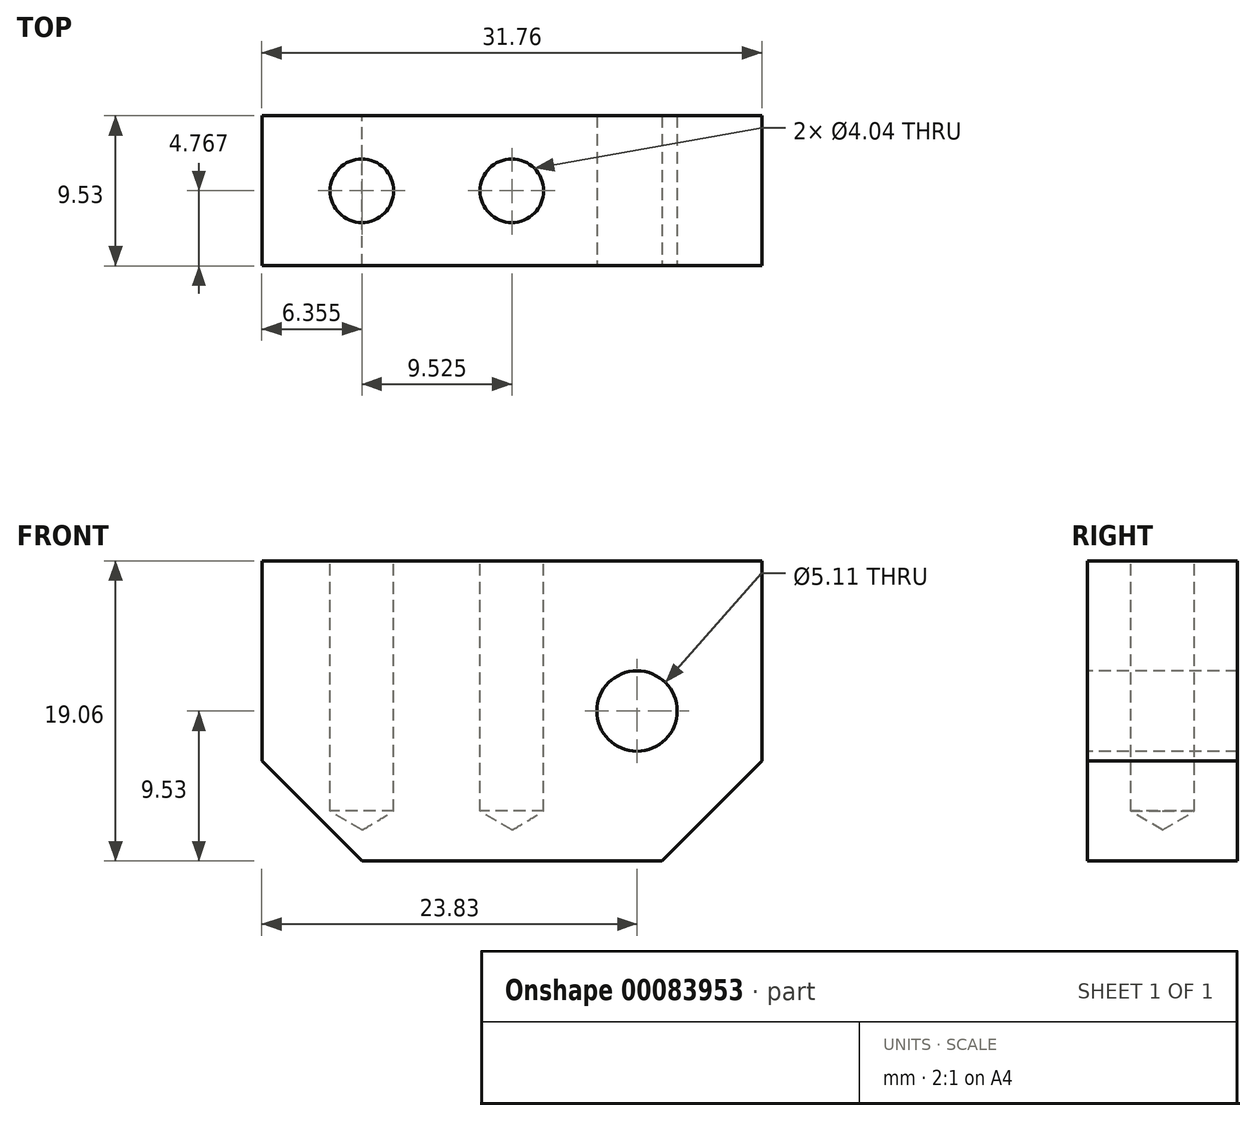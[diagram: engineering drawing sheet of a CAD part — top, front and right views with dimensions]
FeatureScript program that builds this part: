
annotation { "Feature Type Name" : "Feature", "Feature Type Description" : "" }
export const myFeature = defineFeature(function(context is Context, id is Id, definition is map)
    precondition{}
    {
        {
            var Q0;
            Q0=qCreatedBy(makeId("Front.planeOp"),FACE);
            var sketch = newSketch(context, id + "F0", { "sketchPlane" : qUnion([Q0])});
            skLineSegment(sketch, "E0.bottom", {"start": v(15.88, -9.52) * mm, "end": v(-15.88, -9.53) * mm});
            skLineSegment(sketch, "E0.top", {"start": v(15.88, 9.53) * mm, "end": v(-15.88, 9.52) * mm});
            skLineSegment(sketch, "E0.left", {"start": v(15.88, -9.52) * mm, "end": v(15.88, 9.53) * mm});
            skLineSegment(sketch, "E0.right", {"start": v(-15.88, -9.53) * mm, "end": v(-15.88, 9.52) * mm});
            skPoint(sketch, "E0.middle", {"position": v(0, 0) * mm});
            skSolve(sketch);
        }
        {
            var Q0;
            Q0=makeQuery(id+"F0.imprint","IMPRINT",FACE,{"disambiguationData":[TD([[makeQuery(id+"F0.imprint","IMPRINT",EDGE,{"derivedFrom":sQuery(id+"F0.wireOp",EDGE,"E0.bottom")}),-1.0]])]});
            extrude(context, id + "F1", {"entities" : qUnion([Q0]), "depth" : 9.52 * mm});
        }
        {
            var Q0;
            Q0=makeQuery(id+"F1.opExtrude","CAP_FACE",FACE,{"disambiguationData":[OSD([sQuery(id+"F0.wireOp",EDGE,"E0.bottom"),sQuery(id+"F0.wireOp",EDGE,"E0.top"),sQuery(id+"F0.wireOp",EDGE,"E0.left"),sQuery(id+"F0.wireOp",EDGE,"E0.right")])],"isStart":false});
            var sketch = newSketch(context, id + "F2", { "sketchPlane" : qUnion([Q0])});
            skLineSegment(sketch, "E1", {"start": v(7.95, 9.53) * mm, "end": v(7.95, -9.52) * mm, "construction": true});
            skLineSegment(sketch, "E2", {"start": v(-15.88, 0) * mm, "end": v(15.88, 0) * mm, "construction": true});
            skPoint(sketch, "E3", {"position": v(7.95, 0) * mm});
            skSolve(sketch);
        }
        {
            var Q0;
            Q0=sQuery(id+"F2.wireOp",VERTEX,"E3");
            var Q1;
            Q1=makeQuery(id+"F1.opExtrude","SWEPT_BODY",BODY,{"disambiguationData":[OSD([sQuery(id+"F0.wireOp",EDGE,"E0.bottom"),sQuery(id+"F0.wireOp",EDGE,"E0.top"),sQuery(id+"F0.wireOp",EDGE,"E0.left"),sQuery(id+"F0.wireOp",EDGE,"E0.right")])]});
            hole(context, id + "F3", {"style" : HoleStyle.SIMPLE, "endStyle" : HoleEndStyle.THROUGH, "standardTappedOrClearance" : lookupTablePath({ "standard" : "ANSI", "engagement" : "75%", "pitch" : "20 tpi", "size" : "1/4", "type" : "Tapped" }), "standardBlindInLast" : lookupTablePath({ "standard" : "ANSI", "engagement" : "75%", "pitch" : "20 tpi", "size" : "1/4", "type" : "Tapped" }), "holeDiameter" : 5.1 * mm, "locations" : qUnion([Q0]), "scope" : qUnion([Q1]), "isTappedThrough" : true, "majorDiameter" : 6.35 * mm, "showTappedDepth" : true});
        }
        {
            var Q0;
            Q0=makeQuery(id+"F1.opExtrude","SWEPT_FACE",FACE,{"disambiguationData":[OSD([sQuery(id+"F0.wireOp",EDGE,"E0.top")])]});
            var sketch = newSketch(context, id + "F4", { "sketchPlane" : qUnion([Q0])});
            skLineSegment(sketch, "E4", {"start": v(-9.53, 0) * mm, "end": v(-9.53, -9.53) * mm, "construction": true});
            skLineSegment(sketch, "E5", {"start": v(0, 0) * mm, "end": v(0, -9.53) * mm, "construction": true});
            skLineSegment(sketch, "E6", {"start": v(-15.88, -4.76) * mm, "end": v(15.88, -4.76) * mm, "construction": true});
            skPoint(sketch, "E7", {"position": v(-9.53, -4.76) * mm});
            skPoint(sketch, "E8", {"position": v(0, -4.76) * mm});
            skSolve(sketch);
        }
        {
            var Q0;
            Q0=sQuery(id+"F4.wireOp",VERTEX,"E7");
            var Q1;
            Q1=sQuery(id+"F4.wireOp",VERTEX,"E8");
            var Q2;
            Q2=makeQuery(id+"F1.opExtrude","SWEPT_BODY",BODY,{"disambiguationData":[OSD([sQuery(id+"F0.wireOp",EDGE,"E0.bottom"),sQuery(id+"F0.wireOp",EDGE,"E0.top"),sQuery(id+"F0.wireOp",EDGE,"E0.left"),sQuery(id+"F0.wireOp",EDGE,"E0.right")])]});
            hole(context, id + "F5", {"style" : HoleStyle.SIMPLE, "endStyle" : HoleEndStyle.BLIND, "standardTappedOrClearance" : lookupTablePath({ "standard" : "ANSI", "engagement" : "75%", "pitch" : "32 tpi", "size" : "#10", "type" : "Tapped" }), "standardBlindInLast" : lookupTablePath({ "standard" : "ANSI", "engagement" : "75%", "pitch" : "32 tpi", "size" : "#10", "type" : "Tapped" }), "holeDiameter" : 4.04 * mm, "holeDepth" : 15.88 * mm, "locations" : qUnion([Q0, Q1]), "scope" : qUnion([Q2]), "majorDiameter" : 4.83 * mm});
        }
        {
            var Q0;
            Q0=makeQuery(id+"F1.opExtrude","SWEPT_EDGE",EDGE,{"disambiguationData":[OSD([sQuery(id+"F0.wireOp",EDGE,"E0.bottom"),sQuery(id+"F0.wireOp",EDGE,"E0.right")])]});
            var Q1;
            Q1=makeQuery(id+"F1.opExtrude","SWEPT_EDGE",EDGE,{"disambiguationData":[OSD([sQuery(id+"F0.wireOp",EDGE,"E0.bottom"),sQuery(id+"F0.wireOp",EDGE,"E0.left")])]});
            chamfer(context, id + "F6", {"entities" : qUnion([Q0, Q1]), "width" : 6.35 * mm, "tangentPropagation" : true});
        }
    });
